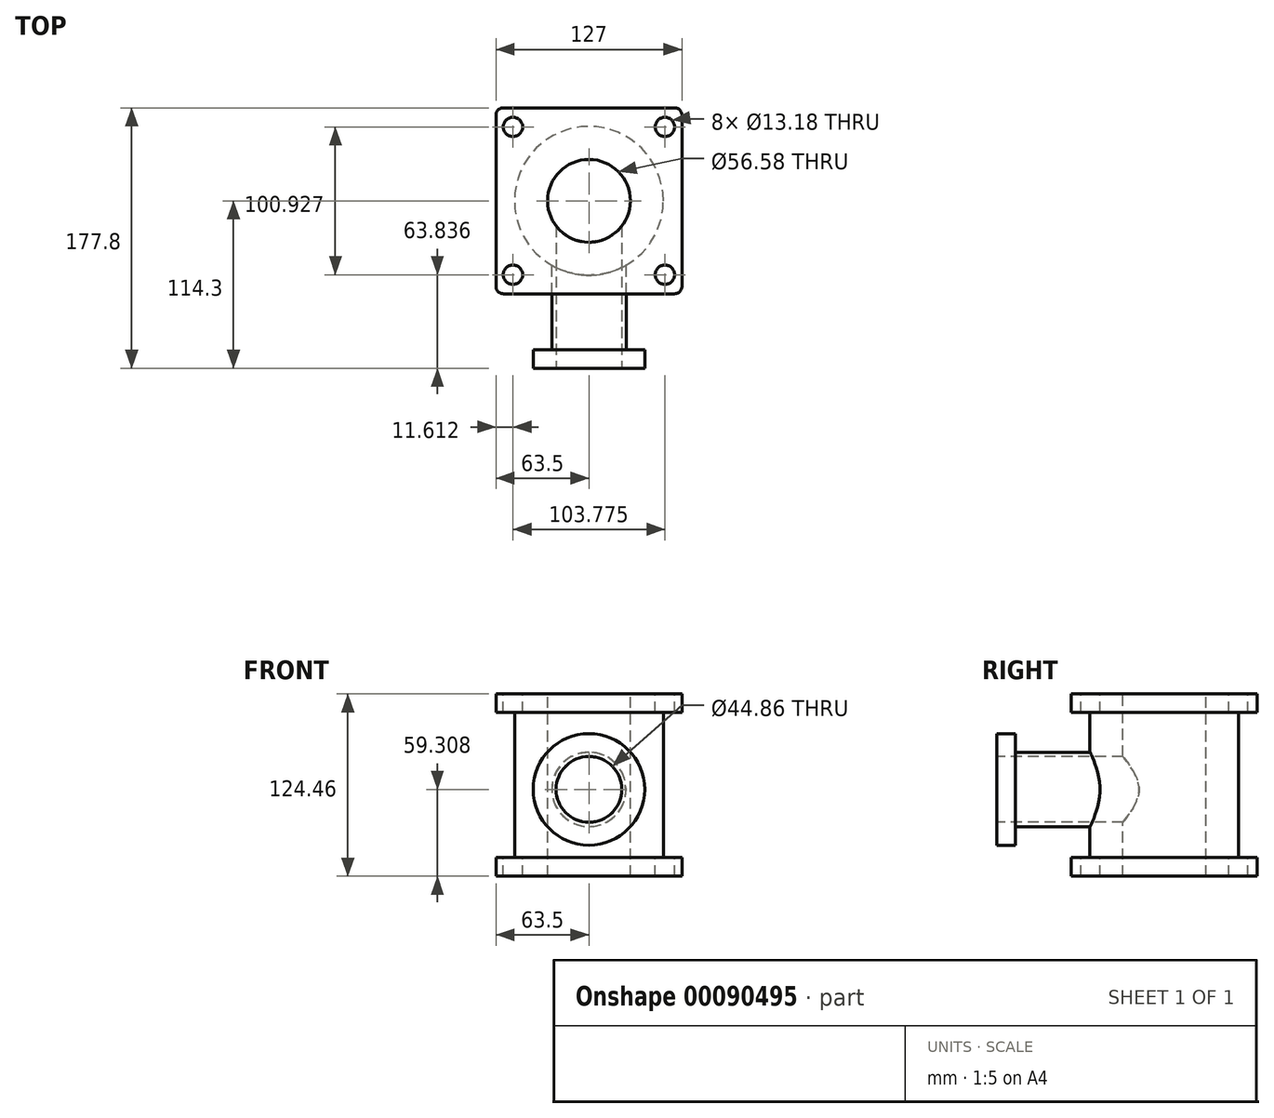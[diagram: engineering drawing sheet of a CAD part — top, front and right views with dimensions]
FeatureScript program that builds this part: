
annotation { "Feature Type Name" : "Feature", "Feature Type Description" : "" }
export const myFeature = defineFeature(function(context is Context, id is Id, definition is map)
    precondition{}
    {
        {
            var Q0;
            Q0=qCreatedBy(makeId("Top.planeOp"),FACE);
            var sketch = newSketch(context, id + "F0", { "sketchPlane" : qUnion([Q0])});
            skLineSegment(sketch, "E0", {"start": v(-63.5, 0) * mm, "end": v(-63.5, 63.5) * mm});
            skLineSegment(sketch, "E1", {"start": v(-63.5, 63.5) * mm, "end": v(0, 63.5) * mm});
            skLineSegment(sketch, "E2.MirrorCS", {"start": v(63.5, 63.5) * mm, "end": v(0, 63.5) * mm});
            skLineSegment(sketch, "E3.MirrorCS", {"start": v(63.5, 0) * mm, "end": v(63.5, 63.5) * mm});
            skLineSegment(sketch, "E4.MirrorCS", {"start": v(-63.5, 0) * mm, "end": v(-63.5, -63.5) * mm});
            skLineSegment(sketch, "E5.MirrorCS", {"start": v(-63.5, -63.5) * mm, "end": v(0, -63.5) * mm});
            skLineSegment(sketch, "E6.MirrorCS", {"start": v(63.5, -63.5) * mm, "end": v(0, -63.5) * mm});
            skLineSegment(sketch, "E7.MirrorCS", {"start": v(63.5, 0) * mm, "end": v(63.5, -63.5) * mm});
            skSolve(sketch);
        }
        {
            var Q0;
            Q0 = qSketchRegion(id + "F0", true);
            extrude(context, id + "F1", {"entities" : qUnion([Q0]), "depth" : 12.7 * mm});
        }
        {
            var Q0;
            Q0=makeQuery(id+"F1.opExtrude","CAP_FACE",FACE,{"disambiguationData":[OSD([sQuery(id+"F0.wireOp",EDGE,"E0"),sQuery(id+"F0.wireOp",EDGE,"E1"),sQuery(id+"F0.wireOp",EDGE,"E2.MirrorCS"),sQuery(id+"F0.wireOp",EDGE,"E3.MirrorCS"),sQuery(id+"F0.wireOp",EDGE,"E4.MirrorCS"),sQuery(id+"F0.wireOp",EDGE,"E5.MirrorCS"),sQuery(id+"F0.wireOp",EDGE,"E6.MirrorCS"),sQuery(id+"F0.wireOp",EDGE,"E7.MirrorCS")])],"isStart":false});
            var sketch = newSketch(context, id + "F2", { "sketchPlane" : qUnion([Q0])});
            skCircle(sketch, "E8", {"center": v(0, 0) * mm, "radius": 50.8 * mm});
            skSolve(sketch);
        }
        {
            var Q0;
            Q0 = qSketchRegion(id + "F2", true);
            extrude(context, id + "F3", {"entities" : qUnion([Q0]), "operationType" : NewBodyOperationType.ADD, "depth" : 99.06 * mm});
        }
        {
            var Q0;
            Q0=makeQuery(id+"F3.opExtrude","CAP_FACE",FACE,{"disambiguationData":[OSD([sQuery(id+"F2.wireOp",EDGE,"E8")])],"isStart":false});
            var sketch = newSketch(context, id + "F4", { "sketchPlane" : qUnion([Q0])});
            skLineSegment(sketch, "E9", {"start": v(-63.5, 0) * mm, "end": v(-63.5, 63.5) * mm});
            skLineSegment(sketch, "E10", {"start": v(-63.5, 63.5) * mm, "end": v(0, 63.5) * mm});
            skLineSegment(sketch, "E11.MirrorCS", {"start": v(63.5, 0) * mm, "end": v(63.5, 63.5) * mm});
            skLineSegment(sketch, "E12.MirrorCS", {"start": v(63.5, 63.5) * mm, "end": v(0, 63.5) * mm});
            skLineSegment(sketch, "E13.MirrorCS", {"start": v(63.5, 0) * mm, "end": v(63.5, -63.5) * mm});
            skLineSegment(sketch, "E14.MirrorCS", {"start": v(-63.5, 0) * mm, "end": v(-63.5, -63.5) * mm});
            skLineSegment(sketch, "E15.MirrorCS", {"start": v(-63.5, -63.5) * mm, "end": v(0, -63.5) * mm});
            skLineSegment(sketch, "E16.MirrorCS", {"start": v(63.5, -63.5) * mm, "end": v(0, -63.5) * mm});
            skSolve(sketch);
        }
        {
            var Q0;
            Q0 = qSketchRegion(id + "F4", true);
            extrude(context, id + "F5", {"entities" : qUnion([Q0]), "operationType" : NewBodyOperationType.ADD, "depth" : 12.7 * mm});
        }
        {
            var Q0;
            Q0=qCreatedBy(makeId("Front.planeOp"),FACE);
            var sketch = newSketch(context, id + "F6", { "sketchPlane" : qUnion([Q0])});
            skCircle(sketch, "E17", {"center": v(0, 59.3) * mm, "radius": 25.4 * mm});
            skSolve(sketch);
        }
        {
            var Q0;
            Q0 = qSketchRegion(id + "F6", true);
            extrude(context, id + "F7", {"entities" : qUnion([Q0]), "operationType" : NewBodyOperationType.ADD, "depth" : 101.6 * mm});
        }
        {
            var Q0;
            Q0=makeQuery(id+"F7.opExtrude","CAP_FACE",FACE,{"disambiguationData":[OSD([sQuery(id+"F6.wireOp",EDGE,"E17")])],"isStart":false});
            var sketch = newSketch(context, id + "F8", { "sketchPlane" : qUnion([Q0])});
            skCircle(sketch, "E18", {"center": v(0, 59.3) * mm, "radius": 38.1 * mm});
            skSolve(sketch);
        }
        {
            var Q0;
            Q0 = qSketchRegion(id + "F8", true);
            extrude(context, id + "F9", {"entities" : qUnion([Q0]), "operationType" : NewBodyOperationType.ADD, "depth" : 12.7 * mm});
        }
        {
            var Q0;
            Q0=makeQuery(id+"F9.opExtrude","CAP_FACE",FACE,{"disambiguationData":[OSD([sQuery(id+"F8.wireOp",EDGE,"E18")])],"isStart":false});
            var sketch = newSketch(context, id + "F10", { "sketchPlane" : qUnion([Q0])});
            skCircle(sketch, "E19", {"center": v(0, 59.3) * mm, "radius": 22.43 * mm});
            skSolve(sketch);
        }
        {
            var Q0;
            Q0 = qSketchRegion(id + "F10", true);
            extrude(context, id + "F11", {"entities" : qUnion([Q0]), "operationType" : NewBodyOperationType.REMOVE, "oppositeDirection" : true, "depth" : 101.6 * mm});
        }
        {
            var Q0;
            Q0=makeQuery(id+"F5.opExtrude","CAP_FACE",FACE,{"disambiguationData":[OSD([sQuery(id+"F4.wireOp",EDGE,"E9"),sQuery(id+"F4.wireOp",EDGE,"E10"),sQuery(id+"F4.wireOp",EDGE,"E11.MirrorCS"),sQuery(id+"F4.wireOp",EDGE,"E12.MirrorCS"),sQuery(id+"F4.wireOp",EDGE,"E13.MirrorCS"),sQuery(id+"F4.wireOp",EDGE,"E14.MirrorCS"),sQuery(id+"F4.wireOp",EDGE,"E15.MirrorCS"),sQuery(id+"F4.wireOp",EDGE,"E16.MirrorCS")])],"isStart":false});
            var sketch = newSketch(context, id + "F12", { "sketchPlane" : qUnion([Q0])});
            skCircle(sketch, "E20", {"center": v(-51.89, 50.46) * mm, "radius": 6.6 * mm});
            skCircle(sketch, "E21.MirrorC", {"center": v(51.89, 50.46) * mm, "radius": 6.6 * mm});
            skCircle(sketch, "E22.MirrorC", {"center": v(51.89, -50.46) * mm, "radius": 6.6 * mm});
            skCircle(sketch, "E23.MirrorC", {"center": v(-51.89, -50.46) * mm, "radius": 6.6 * mm});
            skSolve(sketch);
        }
        {
            var Q0;
            Q0 = qSketchRegion(id + "F12", true);
            extrude(context, id + "F13", {"entities" : qUnion([Q0]), "operationType" : NewBodyOperationType.REMOVE, "endBound" : BoundingType.THROUGH_ALL, "oppositeDirection" : true, "depth" : 25.4 * mm});
        }
        {
            var Q0;
            Q0=makeQuery(id+"F5.opExtrude","SWEPT_EDGE",EDGE,{"disambiguationData":[OSD([sQuery(id+"F4.wireOp",EDGE,"E13.MirrorCS"),sQuery(id+"F4.wireOp",EDGE,"E16.MirrorCS")])]});
            var Q1;
            Q1=makeQuery(id+"F5.opExtrude","SWEPT_EDGE",EDGE,{"disambiguationData":[OSD([sQuery(id+"F4.wireOp",EDGE,"E11.MirrorCS"),sQuery(id+"F4.wireOp",EDGE,"E12.MirrorCS")])]});
            var Q2;
            Q2=makeQuery(id+"F1.opExtrude","SWEPT_EDGE",EDGE,{"disambiguationData":[OSD([sQuery(id+"F0.wireOp",EDGE,"E2.MirrorCS"),sQuery(id+"F0.wireOp",EDGE,"E3.MirrorCS")])]});
            var Q3;
            Q3=makeQuery(id+"F1.opExtrude","SWEPT_EDGE",EDGE,{"disambiguationData":[OSD([sQuery(id+"F0.wireOp",EDGE,"E6.MirrorCS"),sQuery(id+"F0.wireOp",EDGE,"E7.MirrorCS")])]});
            var Q4;
            Q4=makeQuery(id+"F5.opExtrude","SWEPT_EDGE",EDGE,{"disambiguationData":[OSD([sQuery(id+"F4.wireOp",EDGE,"E14.MirrorCS"),sQuery(id+"F4.wireOp",EDGE,"E15.MirrorCS")])]});
            var Q5;
            Q5=makeQuery(id+"F1.opExtrude","SWEPT_EDGE",EDGE,{"disambiguationData":[OSD([sQuery(id+"F0.wireOp",EDGE,"E4.MirrorCS"),sQuery(id+"F0.wireOp",EDGE,"E5.MirrorCS")])]});
            var Q6;
            Q6=makeQuery(id+"F5.opExtrude","SWEPT_EDGE",EDGE,{"disambiguationData":[OSD([sQuery(id+"F4.wireOp",EDGE,"E9"),sQuery(id+"F4.wireOp",EDGE,"E10")])]});
            var Q7;
            Q7=makeQuery(id+"F1.opExtrude","SWEPT_EDGE",EDGE,{"disambiguationData":[OSD([sQuery(id+"F0.wireOp",EDGE,"E0"),sQuery(id+"F0.wireOp",EDGE,"E1")])]});
            fillet(context, id + "F14", {"entities" : qUnion([Q0, Q1, Q2, Q3, Q4, Q5, Q6, Q7]), "radius" : 5.08 * mm, "tangentPropagation" : true, "allowEdgeOverflow" : false});
        }
        {
            var Q0;
            Q0=makeQuery(id+"F5.opExtrude","CAP_FACE",FACE,{"disambiguationData":[OSD([sQuery(id+"F4.wireOp",EDGE,"E9"),sQuery(id+"F4.wireOp",EDGE,"E10"),sQuery(id+"F4.wireOp",EDGE,"E11.MirrorCS"),sQuery(id+"F4.wireOp",EDGE,"E12.MirrorCS"),sQuery(id+"F4.wireOp",EDGE,"E13.MirrorCS"),sQuery(id+"F4.wireOp",EDGE,"E14.MirrorCS"),sQuery(id+"F4.wireOp",EDGE,"E15.MirrorCS"),sQuery(id+"F4.wireOp",EDGE,"E16.MirrorCS")])],"isStart":false});
            var sketch = newSketch(context, id + "F15", { "sketchPlane" : qUnion([Q0])});
            skCircle(sketch, "E24", {"center": v(0, 0) * mm, "radius": 28.29 * mm});
            skSolve(sketch);
        }
        {
            var Q0;
            Q0 = qSketchRegion(id + "F15", true);
            extrude(context, id + "F16", {"entities" : qUnion([Q0]), "operationType" : NewBodyOperationType.REMOVE, "endBound" : BoundingType.THROUGH_ALL, "oppositeDirection" : true, "depth" : 73.66 * mm});
        }
    });
